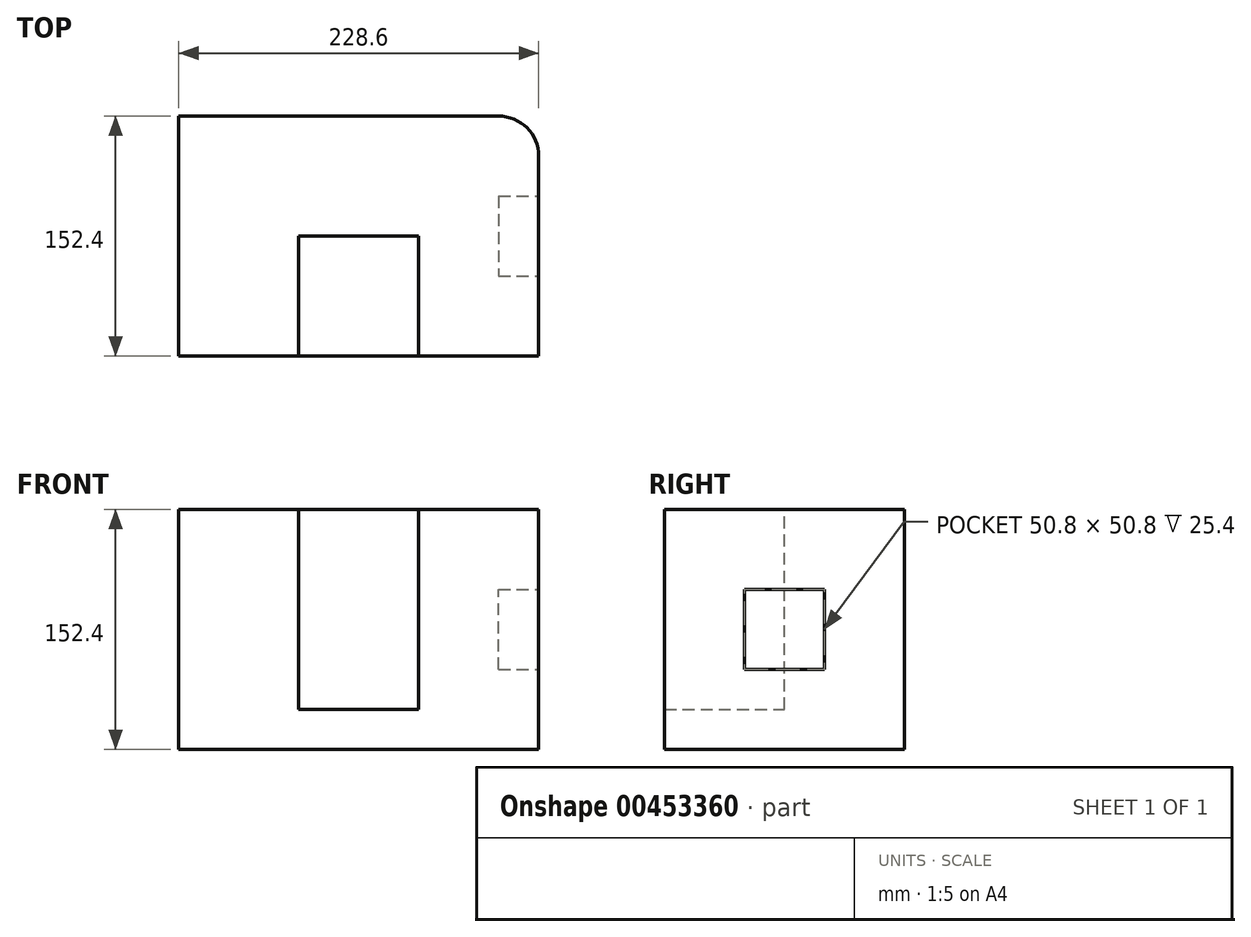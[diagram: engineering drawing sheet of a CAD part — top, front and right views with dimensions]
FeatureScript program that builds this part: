
annotation { "Feature Type Name" : "Feature", "Feature Type Description" : "" }
export const myFeature = defineFeature(function(context is Context, id is Id, definition is map)
    precondition{}
    {
        {
            var Q0;
            Q0=qCreatedBy(makeId("Front.planeOp"),FACE);
            var sketch = newSketch(context, id + "F0", { "sketchPlane" : qUnion([Q0])});
            skLineSegment(sketch, "E0", {"start": v(114.3, -76.2) * mm, "end": v(-114.3, -76.2) * mm});
            skLineSegment(sketch, "E1", {"start": v(-114.3, -76.2) * mm, "end": v(-114.3, 76.2) * mm});
            skLineSegment(sketch, "E2.MirrorCS", {"start": v(114.3, -76.2) * mm, "end": v(114.3, 76.2) * mm});
            skLineSegment(sketch, "E3.MirrorCS", {"start": v(114.3, 76.2) * mm, "end": v(-114.3, 76.2) * mm});
            skSolve(sketch);
        }
        {
            var Q0;
            Q0=makeQuery(id+"F0.imprint","IMPRINT",FACE,{"disambiguationData":[TD([[makeQuery(id+"F0.imprint","IMPRINT",EDGE,{"derivedFrom":sQuery(id+"F0.wireOp",EDGE,"E0")}),-1.0]])]});
            extrude(context, id + "F1", {"entities" : qUnion([Q0]), "endBound" : BoundingType.SYMMETRIC, "depth" : 152.4 * mm});
        }
        {
            var Q0;
            Q0=makeQuery(id+"F1.opExtrude","SWEPT_FACE",FACE,{"disambiguationData":[OSD([sQuery(id+"F0.wireOp",EDGE,"E3.MirrorCS")])]});
            var sketch = newSketch(context, id + "F2", { "sketchPlane" : qUnion([Q0])});
            skLineSegment(sketch, "E4", {"start": v(-38.1, -76.2) * mm, "end": v(38.1, -76.2) * mm});
            skLineSegment(sketch, "E5", {"start": v(-38.1, -76.2) * mm, "end": v(-38.1, 0) * mm});
            skLineSegment(sketch, "E6.MirrorCS", {"start": v(38.1, -76.2) * mm, "end": v(38.1, 0) * mm});
            skLineSegment(sketch, "E7", {"start": v(-38.1, 0) * mm, "end": v(38.1, 0) * mm});
            skSolve(sketch);
        }
        {
            var Q0;
            Q0=makeQuery(id+"F2.imprint","IMPRINT",FACE,{"disambiguationData":[TD([[makeQuery(id+"F2.imprint","IMPRINT",EDGE,{"derivedFrom":sQuery(id+"F2.wireOp",EDGE,"E4")}),-1.0]])]});
            extrude(context, id + "F3", {"entities" : qUnion([Q0]), "operationType" : NewBodyOperationType.REMOVE, "oppositeDirection" : true, "depth" : 127 * mm});
        }
        {
            var Q0;
            Q0=makeQuery(id+"F1.opExtrude","CAP_EDGE",EDGE,{"disambiguationData":[OSD([sQuery(id+"F0.wireOp",EDGE,"E2.MirrorCS")])],"isStart":true});
            fillet(context, id + "F4", {"entities" : qUnion([Q0]), "radius" : 25.4 * mm, "tangentPropagation" : true, "allowEdgeOverflow" : false});
        }
        {
            var Q0;
            Q0=makeQuery(id+"F1.opExtrude","SWEPT_FACE",FACE,{"disambiguationData":[OSD([sQuery(id+"F0.wireOp",EDGE,"E2.MirrorCS")])]});
            var sketch = newSketch(context, id + "F5", { "sketchPlane" : qUnion([Q0])});
            skLineSegment(sketch, "E8", {"start": v(25.4, -25.4) * mm, "end": v(25.4, 25.4) * mm});
            skLineSegment(sketch, "E9", {"start": v(25.4, 25.4) * mm, "end": v(-25.4, 25.4) * mm});
            skLineSegment(sketch, "E10", {"start": v(25.4, -25.4) * mm, "end": v(-25.4, -25.4) * mm});
            skLineSegment(sketch, "E11", {"start": v(-25.4, -25.4) * mm, "end": v(-25.4, 25.4) * mm});
            skSolve(sketch);
        }
        {
            var Q0;
            Q0=makeQuery(id+"F5.imprint","IMPRINT",FACE,{"disambiguationData":[TD([[makeQuery(id+"F5.imprint","IMPRINT",EDGE,{"derivedFrom":sQuery(id+"F5.wireOp",EDGE,"E8")}),1.0]])]});
            extrude(context, id + "F6", {"entities" : qUnion([Q0]), "operationType" : NewBodyOperationType.REMOVE, "oppositeDirection" : true, "depth" : 25.4 * mm});
        }
    });
